FCSTD DOCUMENT  (FreeCAD 1.0R39319 (Git))
Label: Assy_Screen_PiTracIRLED
License: All rights reserved
LicenseURL: https://en.wikipedia.org/wiki/All_rights_reserved
objects: App::DocumentObjectGroup×3, App::Link×3, PartDesign::CoordinateSystem×1, App::FeaturePython×1, App::Part×1, TechDraw::DrawSVGTemplate×1, TechDraw::DrawProjGroupItem×1, TechDraw::DrawPage×1
note: 1 computed .brp shape members not serialized (recipe doc carries the construction recipe); baked Part::Feature solids carry a one-line shape summary decoded from their .brp
EXTERNAL_REF file=Assy_PiTracIRLED.FCStd obj=LCS_Origin
EXTERNAL_REF file=Assy_PiTracIRLED.FCStd obj=Assembly
EXTERNAL_REF file=Assy_EyeScreen.FCStd obj=LCS_Origin
EXTERNAL_REF file=Assy_EyeScreen.FCStd obj=Assembly
EXTERNAL_REF file=Assy_EyeScreen_Clamp.FCStd obj=LCS_Origin
EXTERNAL_REF file=Assy_EyeScreen_Clamp.FCStd obj=Assembly

FEATURE [App::DocumentObjectGroup] Parts
FEATURE [PartDesign::CoordinateSystem] LCS_Origin
  AttacherType = Attacher::AttachEngine3D
  AttachmentSupport = -> [X_Axis]
  MapMode = 2
FEATURE [App::DocumentObjectGroup] Constraints
FEATURE [App::FeaturePython] Variables  # WARN: FeaturePython — macro-defined, semantics opaque (R4)
  Type = App::PropertyContainer
FEATURE [App::DocumentObjectGroup] Configurations
FEATURE [App::Link] Assy_PiTracIRLED
  AttachedBy = #LCS_Origin
  AttachedTo = Parent Assembly#LCS_Origin
  LinkedObject = -> <external Assy_PiTracIRLED.FCStd>#Assembly
  SolverId = Asm4EE
  expr: Placement = LCS_Origin.Placement * AttachmentOffset * Assy_PiTracIRLED#LCS_Origin.Placement ^ -1
FEATURE [App::Link] Assy_EyeScreen
  AttachedBy = #LCS_Origin
  AttachedTo = Parent Assembly#LCS_Origin
  AttachmentOffset = pos=(0,0,0) rot=(0.707107,0,0.707107;3.14159rad)
  LinkPlacement = pos=(0,0,0) rot=(0.707107,0,0.707107;3.14159rad)
  LinkedObject = -> <external Assy_EyeScreen.FCStd>#Assembly
  Placement = pos=(0,0,0) rot=(0.707107,0,0.707107;3.14159rad)
  SolverId = Asm4EE
  expr: Placement = LCS_Origin.Placement * AttachmentOffset * Assy_EyeScreen#LCS_Origin.Placement ^ -1
FEATURE [App::Link] Assy_EyeScreen_Clamp
  AttachedBy = #LCS_Origin
  AttachedTo = Parent Assembly#LCS_Origin
  AttachmentOffset = pos=(0,0,0) rot=(0.707107,-0.707107,0;3.14159rad)
  LinkPlacement = pos=(0,0,0) rot=(0.707107,-0.707107,0;3.14159rad)
  LinkedObject = -> <external Assy_EyeScreen_Clamp.FCStd>#Assembly
  Placement = pos=(0,0,0) rot=(0.707107,-0.707107,0;3.14159rad)
  SolverId = Asm4EE
  expr: Placement = LCS_Origin.Placement * AttachmentOffset * Assy_EyeScreen_Clamp#LCS_Origin.Placement ^ -1
FEATURE [App::Part] Assembly  label="Assy_Screen_PiTracIRLED"
  AssemblyType = Part::Link
  Group = -> [LCS_Origin,Constraints,Variables,Configurations,Assy_PiTracIRLED,Assy_EyeScreen,Assy_EyeScreen_Clamp]
  Origin = -> Origin
  Type = Assembly
FEATURE [TechDraw::DrawSVGTemplate] Template
  Height = 210
  Orientation = 1
  Template = C:/Program Files/FreeCAD 1.0/data/Mod/TechDraw/Templates/Default_Template_A4_Landscape.svg
  Width = 297
FEATURE [TechDraw::DrawProjGroupItem] View
  CoarseView = false
  Direction = (0.57735,-0.57735,0.57735)
  Focus = 100
  HardHidden = false
  IsoCount = 0
  IsoHidden = false
  IsoVisible = false
  LockPosition = false
  Perspective = false
  Rotation = 0
  RotationVector = (1,0,0)
  ScaleType = 0
  ScrubCount = 1
  SeamHidden = false
  SeamVisible = false
  SmoothHidden = false
  SmoothVisible = true
  Source = -> [Assembly]
  Type = 0
  X = 148.5
  XDirection = (-5.7735e-07,-0.707107,-0.707107)
  Y = 105
FEATURE [TechDraw::DrawPage] Page
  KeepUpdated = true
  NextBalloonIndex = 1
  ProjectionType = 0
  Template = -> Template
  Views = -> [View]

RESOLVED EXTERNAL PARTS (link-assembly join: the EXTERNAL_REF files above that resolve inside this repo's crawl, each included once):
---- part Assy_PiTracIRLED.FCStd = doc fcstd_29a45dd05467 ----
FCSTD DOCUMENT  (FreeCAD 1.0R39319 (Git))
Label: Assy_PiTracIRLED
License: All rights reserved
LicenseURL: https://en.wikipedia.org/wiki/All_rights_reserved
objects: TechDraw::DrawProjGroupItem×7, TechDraw::DrawViewBalloon×4, App::DocumentObjectGroup×3, App::Link×2, TechDraw::DrawSVGTemplate×2, Part::FeaturePython×2, TechDraw::DrawViewDimension×2, TechDraw::DrawPage×2, PartDesign::CoordinateSystem×1, App::FeaturePython×1, Spreadsheet::Sheet×1, TechDraw::DrawViewSpreadsheet×1, App::Part×1, TechDraw::DrawProjGroup×1
note: 6 computed .brp shape members not serialized (recipe doc carries the construction recipe); baked Part::Feature solids carry a one-line shape summary decoded from their .brp
EXTERNAL_REF file=../../Part/Print/5x2IRLED_Eyeball.FCStd obj=center
EXTERNAL_REF file=../../Part/Print/5x2IRLED_Eyeball.FCStd obj=Part
EXTERNAL_REF file=../../Part/Purchase/IRLED.FCStd obj=LCS_1
EXTERNAL_REF file=../../Part/Print/5x2IRLED_Eyeball.FCStd obj=LCS_1
EXTERNAL_REF file=../../Part/Purchase/IRLED.FCStd obj=IRLED_Only_1

FEATURE [App::DocumentObjectGroup] Parts
FEATURE [PartDesign::CoordinateSystem] LCS_Origin
  AttacherType = Attacher::AttachEngine3D
  AttachmentSupport = -> [X_Axis]
  MapMode = 2
FEATURE [App::DocumentObjectGroup] Constraints
FEATURE [App::FeaturePython] Variables  # WARN: FeaturePython — macro-defined, semantics opaque (R4)
  Type = App::PropertyContainer
FEATURE [App::DocumentObjectGroup] Configurations
FEATURE [App::Link] _x2IRLED_Eyeball  label="5x2IRLED_Eyeball"
  AttachedBy = #center
  AttachedTo = Parent Assembly#LCS_Origin
  LinkedObject = -> <external ../../Part/Print/5x2IRLED_Eyeball.FCStd>#Part
  SolverId = Asm4EE
  expr: Placement = LCS_Origin.Placement * AttachmentOffset * _x2IRLED_Eyeball#center.Placement ^ -1
FEATURE [App::Link] IRLED_Only_1  label="IRLED Only 1"
  AttachedBy = #LCS_1
  AttachedTo = _x2IRLED_Eyeball#LCS_1
  LinkPlacement = pos=(12.4672,17.5,0.0506) rot=(0,0,-1;1.5708rad)
  LinkedObject = -> <external ../../Part/Purchase/IRLED.FCStd>#IRLED_Only_1
  Placement = pos=(12.4672,17.5,0.0506) rot=(0,0,-1;1.5708rad)
  SolverId = Asm4EE
  expr: Placement = _x2IRLED_Eyeball.Placement * _x2IRLED_Eyeball#LCS_1.Placement * AttachmentOffset * IRLED#LCS_1.Placement ^ -1
FEATURE [TechDraw::DrawSVGTemplate] Template
  EditableTexts = approval_person=GitHub PR; creator=Stefan; date_of_issue=20.03.2026; document_type=Assembly Drawing; general_tolerances=na; identification_number=na; language_code=EN; part_material=na; revision_index=AAA; scale=1 : 1; sheet_number=1 / 1; title=Assy_PiTracIRLED
  Height = 297
  Orientation = 1
  Template = <userpath>/Documents/PiTrac/3D Printed Parts/Enclosure Version 3/Assets/PiTrac_A3_Landscape_ISO5457_minimal.svg
  Width = 420
FEATURE [Spreadsheet::Sheet] Spreadsheet  label="BOM"
  cells = A1=3; B1=2; C1='M3x10 mm self-tapping screw; D1='8-12 mm ; A2=2; B2=1; C2='5x2 IR LED board; D2='-; A3=1; B3=1; C3='5x2IRLED_Eyeball; D3='-; E3='PETG or PLA; A4='Position; B4='Quantity; C4='Part; D4='Dimensions; E4='Material
FEATURE [TechDraw::DrawViewSpreadsheet] Sheet
  CellEnd = E4
  CellStart = A1
  Font = osifont
  LineWidth = 0.35
  LockPosition = false
  Rotation = 0
  ScaleType = 2
  Source = -> Spreadsheet
  Symbol = <blob: 4584 chars omitted>
  TextSize = 12
  X = 324.475
  Y = 95.4404
FEATURE [Part::FeaturePython] Screw  label="ST2.9x9.5-Screw"  # WARN: FeaturePython — macro-defined, semantics opaque (R4)
  BaseObject = -> IRLED_Only_1 [Part__Feature067.Edge20]
  Diameter = 2
  Invert = false
  LeftHanded = false
  Length = 1
  LengthCustom = 9.5
  MatchOuter = false
  OffsetAngle = 0
  Placement = pos=(8.7,0,0.8124) rot=(0,0,1;0rad)
  Thread = false
  Type = 81
FEATURE [Part::FeaturePython] Screw001  label="ST2.9x9.5-Screw001"  # WARN: FeaturePython — macro-defined, semantics opaque (R4)
  BaseObject = -> IRLED_Only_1 [Part__Feature067.Edge17]
  Diameter = 2
  Invert = false
  LeftHanded = false
  Length = 1
  LengthCustom = 9.5
  MatchOuter = false
  OffsetAngle = 0
  Placement = pos=(-8.699,3.6e-15,0.8124) rot=(0,0,1;0rad)
  Thread = false
  Type = 81
FEATURE [App::Part] Assembly  label="Assy_PiTracIRLED"
  AssemblyType = Part::Link
  Group = -> [LCS_Origin,Constraints,Variables,Configurations,_x2IRLED_Eyeball,IRLED_Only_1,Screw,Screw001]
  Origin = -> Origin
  Type = Assembly
FEATURE [TechDraw::DrawProjGroupItem] ProjItem  label="Top"
  CoarseView = false
  Direction = (1,0,0)
  Focus = 100
  HardHidden = false
  IsoCount = 0
  IsoHidden = false
  IsoVisible = false
  LockPosition = false
  Perspective = false
  Rotation = 0
  RotationVector = (1,0,0)
  ScaleType = 0
  ScrubCount = 1
  SeamHidden = false
  SeamVisible = false
  SmoothHidden = false
  SmoothVisible = true
  Source = -> [Assembly]
  Type = 4
  X = 0
  XDirection = (0,-1,0)
  Y = -67
FEATURE [TechDraw::DrawProjGroupItem] View
  CoarseView = false
  Direction = (0.57735,-0.57735,0.57735)
  Focus = 100
  HardHidden = false
  IsoCount = 0
  IsoHidden = false
  IsoVisible = false
  LockPosition = false
  Perspective = false
  Rotation = 0
  RotationVector = (1,0,0)
  ScaleType = 0
  ScrubCount = 1
  SeamHidden = false
  SeamVisible = false
  SmoothHidden = false
  SmoothVisible = true
  Source = -> [Assembly]
  Type = 0
  X = 187.439
  XDirection = (-5.7735e-07,-0.707107,-0.707107)
  Y = 69.9551
FEATURE [TechDraw::DrawProjGroupItem] View001  label="Front"
  CoarseView = false
  Direction = (0,0,1)
  Focus = 100
  HardHidden = false
  IsoCount = 0
  IsoHidden = false
  IsoVisible = false
  LockPosition = true
  Perspective = false
  Rotation = 0
  RotationVector = (1,0,0)
  ScaleType = 2
  ScrubCount = 1
  SeamHidden = false
  SeamVisible = false
  SmoothHidden = false
  SmoothVisible = true
  Source = -> [Assembly]
  Type = 0
  X = 0
  XDirection = (0,-1,0)
  Y = 0
FEATURE [TechDraw::DrawProjGroupItem] ProjItem001  label="Top001"
  CoarseView = false
  Direction = (1,0,0)
  Focus = 100
  HardHidden = false
  IsoCount = 0
  IsoHidden = false
  IsoVisible = false
  LockPosition = false
  Perspective = false
  Rotation = 0
  RotationVector = (1,0,0)
  ScaleType = 0
  ScrubCount = 1
  SeamHidden = false
  SeamVisible = false
  SmoothHidden = false
  SmoothVisible = true
  Source = -> [Assembly]
  Type = 4
  X = 0
  XDirection = (0,-1,0)
  Y = -67
FEATURE [TechDraw::DrawProjGroupItem] ProjItem002  label="Left"
  CoarseView = false
  Direction = (0,1,1e-16)
  Focus = 100
  HardHidden = false
  IsoCount = 0
  IsoHidden = false
  IsoVisible = false
  LockPosition = false
  Perspective = false
  Rotation = 0
  RotationVector = (1,0,0)
  ScaleType = 0
  ScrubCount = 1
  SeamHidden = false
  SeamVisible = false
  SmoothHidden = false
  SmoothVisible = true
  Source = -> [Assembly]
  Type = 1
  X = 67
  XDirection = (0,-1e-16,1)
  Y = 0
FEATURE [TechDraw::DrawProjGroupItem] ProjItem003  label="Rear"
  CoarseView = false
  Direction = (0,0,-1)
  Focus = 100
  HardHidden = false
  IsoCount = 0
  IsoHidden = false
  IsoVisible = false
  LockPosition = false
  Perspective = false
  Rotation = 0
  RotationVector = (1,0,0)
  ScaleType = 0
  ScrubCount = 1
  SeamHidden = false
  SeamVisible = false
  SmoothHidden = false
  SmoothVisible = true
  Source = -> [Assembly]
  Type = 3
  X = 134
  XDirection = (0,1,0)
  Y = 0
FEATURE [TechDraw::DrawProjGroup] ProjGroup
  Anchor = -> View001
  AutoDistribute = true
  LockPosition = false
  ProjectionType = 0
  Rotation = 0
  ScaleType = 0
  Source = -> [Assembly]
  Views = -> [View001,ProjItem001,ProjItem002,ProjItem003]
  X = 92.1827
  Y = 215.347
  spacingX = 15
  spacingY = 15
FEATURE [TechDraw::DrawViewBalloon] Balloon
  BubbleShape = 0
  EndType = 0
  EndTypeScale = 1
  KinkLength = 5
  LockPosition = false
  OriginX = -28.2605
  OriginY = -17.3134
  Rotation = 0
  ScaleType = 0
  ShapeScale = 1
  SourceView = -> View001
  Text = 1
  TextWrapLen = -1
  X = -55
  Y = -28.23
FEATURE [TechDraw::DrawViewBalloon] Balloon001
  BubbleShape = 0
  EndType = 0
  EndTypeScale = 1
  KinkLength = 5
  LockPosition = false
  OriginX = -15.7268
  OriginY = 2.32286
  Rotation = 0
  ScaleType = 0
  ShapeScale = 1
  SourceView = -> View001
  Text = 2
  TextWrapLen = -1
  X = -55
  Y = 18.5627
FEATURE [TechDraw::DrawViewBalloon] Balloon002
  BubbleShape = 0
  EndType = 0
  EndTypeScale = 1
  KinkLength = 5
  LockPosition = false
  OriginX = -1.10408
  OriginY = -9.79311
  Rotation = 0
  ScaleType = 0
  ShapeScale = 1
  SourceView = -> View001
  Text = 3
  TextWrapLen = -1
  X = -55
  Y = -7.75816
FEATURE [TechDraw::DrawViewBalloon] Balloon003
  BubbleShape = 0
  EndType = 0
  EndTypeScale = 1
  KinkLength = 5
  LockPosition = false
  OriginX = -0.205
  OriginY = 9.27105
  Rotation = 0
  ScaleType = 0
  ShapeScale = 1
  SourceView = -> View001
  Text = 3
  TextWrapLen = -1
  X = -55
  Y = 39.7159
FEATURE [TechDraw::DrawViewDimension] Dimension
  AngleOverride = false
  Arbitrary = false
  ArbitraryTolerances = false
  BoxCorners = (2) [(-12,-40,-1e-07),(12,40,1e-07)]
  EqualTolerance = true
  ExtensionAngle = 0
  FormatSpec = %.2w
  FormatSpecOverTolerance = %+.2w
  FormatSpecUnderTolerance = %+.2w
  Inverted = false
  LineAngle = 0
  LockPosition = false
  MeasureType = 1
  OverTolerance = 0
  References2D = -> [ProjItem002]
  Rotation = 0
  ScaleType = 0
  TheoreticalExact = false
  Type = 0
  UnderTolerance = 0
  X = 0
  Y = 57.6927
FEATURE [TechDraw::DrawViewDimension] Dimension001
  AngleOverride = false
  Arbitrary = false
  ArbitraryTolerances = false
  BoxCorners = (2) [(-40,-40,0),(40,40,0)]
  EqualTolerance = true
  ExtensionAngle = 0
  FormatSpec = ⌀%.2w
  FormatSpecOverTolerance = %+.2w
  FormatSpecUnderTolerance = %+.2w
  Inverted = false
  LineAngle = 0
  LockPosition = false
  MeasureType = 1
  OverTolerance = 0
  References2D = -> [ProjItem003]
  Rotation = 0
  ScaleType = 0
  TheoreticalExact = false
  Type = 5
  UnderTolerance = 0
  X = 65.2263
  Y = 46.4264
FEATURE [TechDraw::DrawPage] Page
  KeepUpdated = true
  NextBalloonIndex = 8
  ProjectionType = 0
  Template = -> Template
  Views = -> [Sheet,View,ProjGroup,Balloon,Balloon001,Balloon002,Balloon003,Dimension,Dimension001]
FEATURE [TechDraw::DrawSVGTemplate] Template001
  Height = 210
  Orientation = 1
  Template = C:/Program Files/FreeCAD 1.0/data/Mod/TechDraw/Templates/Default_Template_A4_Landscape.svg
  Width = 297
FEATURE [TechDraw::DrawProjGroupItem] View002
  CoarseView = false
  Direction = (0.57735,-0.57735,0.57735)
  Focus = 100
  HardHidden = false
  IsoCount = 0
  IsoHidden = false
  IsoVisible = false
  LockPosition = false
  Perspective = false
  Rotation = 0
  RotationVector = (1,0,0)
  Scale = 2
  ScaleType = 2
  ScrubCount = 1
  SeamHidden = false
  SeamVisible = false
  SmoothHidden = false
  SmoothVisible = true
  Source = -> [Assembly]
  Type = 0
  X = 148.5
  XDirection = (-5.7735e-07,-0.707107,-0.707107)
  Y = 105
FEATURE [TechDraw::DrawPage] Page001
  KeepUpdated = true
  NextBalloonIndex = 1
  ProjectionType = 0
  Template = -> Template001
  Views = -> [View002]
